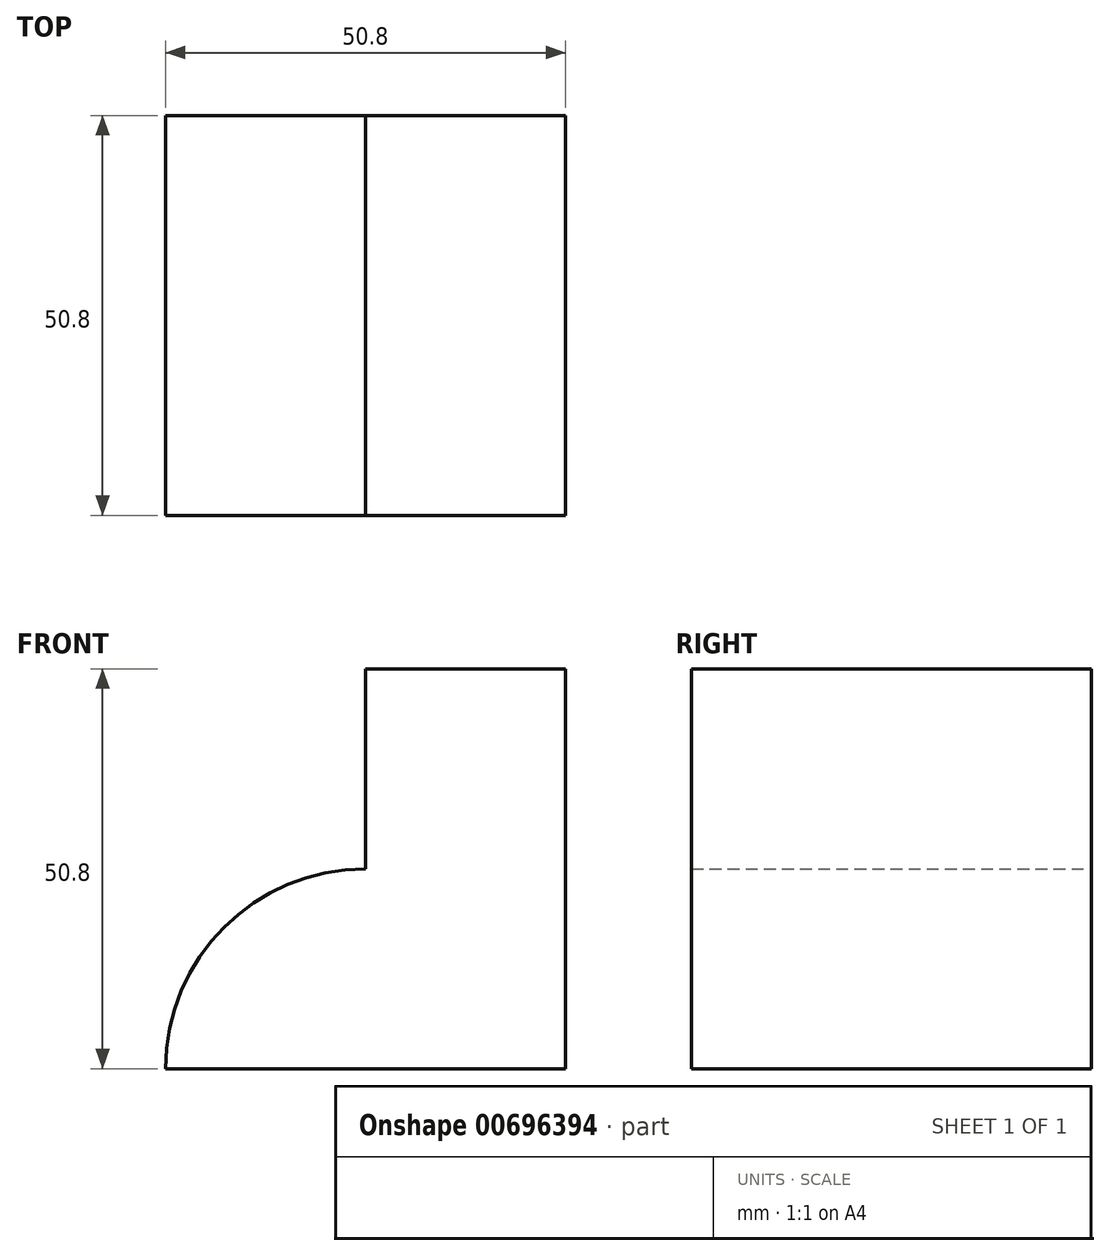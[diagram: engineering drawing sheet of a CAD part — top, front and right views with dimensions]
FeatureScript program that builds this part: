
annotation { "Feature Type Name" : "Feature", "Feature Type Description" : "" }
export const myFeature = defineFeature(function(context is Context, id is Id, definition is map)
    precondition{}
    {
        {
            var Q0;
            Q0=qCreatedBy(makeId("Front.planeOp"),FACE);
            var sketch = newSketch(context, id + "F0", { "sketchPlane" : qUnion([Q0])});
            skLineSegment(sketch, "E0", {"start": v(0, 0) * mm, "end": v(0, 50.8) * mm});
            skLineSegment(sketch, "E1", {"start": v(0, 0) * mm, "end": v(-50.8, 0) * mm});
            skLineSegment(sketch, "E2", {"start": v(0, 50.8) * mm, "end": v(-25.4, 50.8) * mm});
            skLineSegment(sketch, "E3", {"start": v(-25.4, 50.8) * mm, "end": v(-25.4, 25.4) * mm});
            skArc(sketch, "E4", {"start": v(-25.4, 25.4) * mm, "mid": v(-43.36, 17.96) * mm, "end": v(-50.8, 0) * mm});
            skSolve(sketch);
        }
        {
            var Q0;
            Q0=makeQuery(id+"F0.imprint","IMPRINT",FACE,{"disambiguationData":[TD([[makeQuery(id+"F0.imprint","IMPRINT",EDGE,{"derivedFrom":sQuery(id+"F0.wireOp",EDGE,"E0")}),1.0]])]});
            extrude(context, id + "F1", {"entities" : qUnion([Q0]), "depth" : 50.8 * mm, "offsetDistance" : 25.4 * mm});
        }
    });
